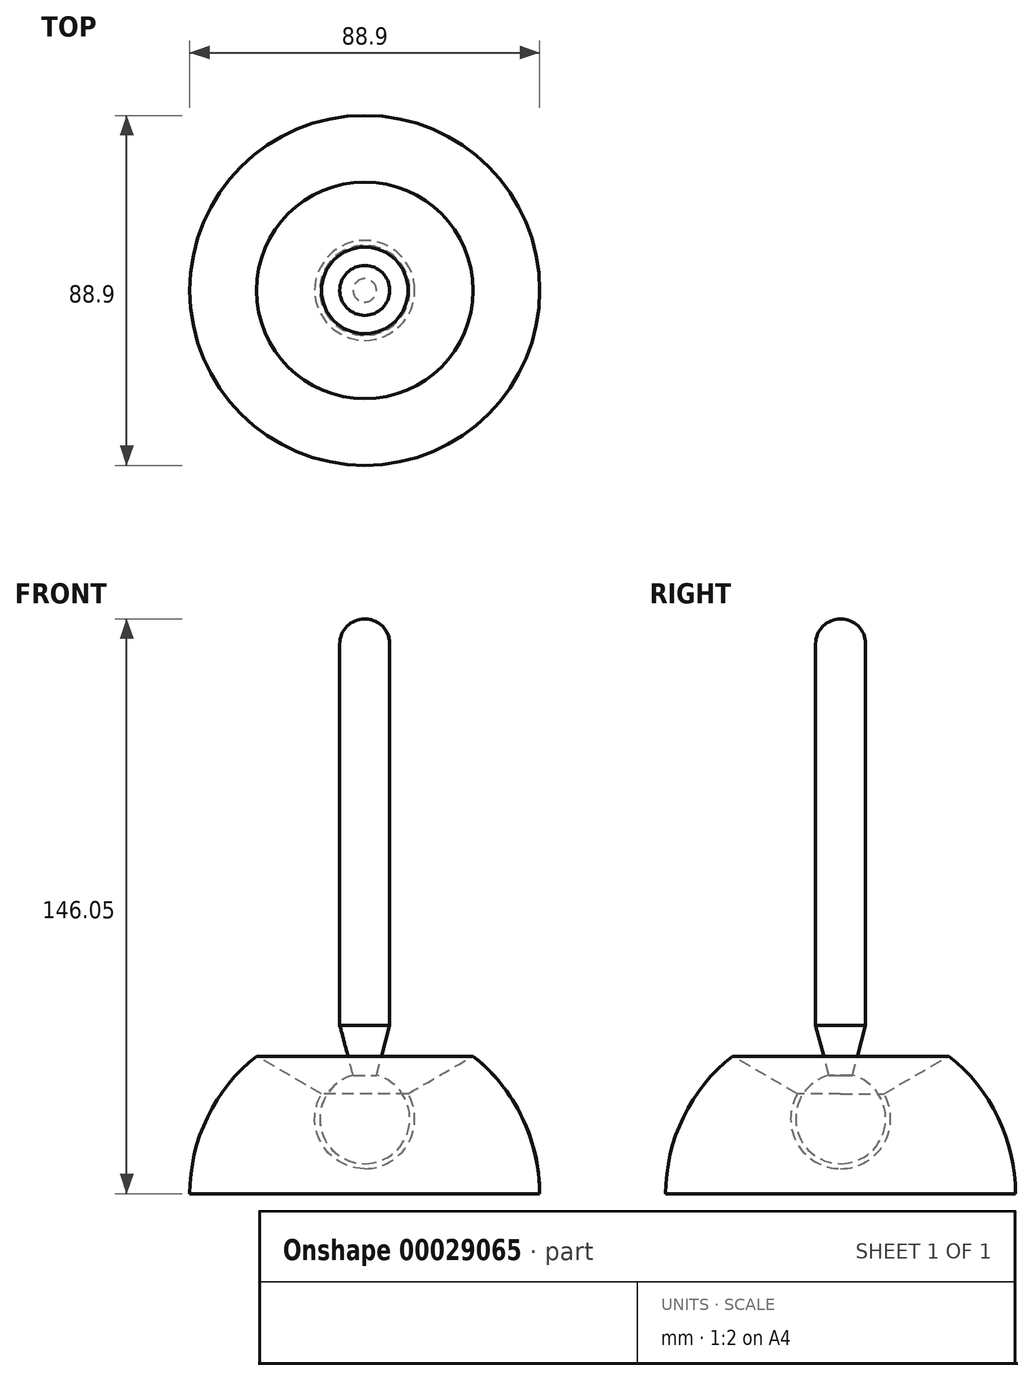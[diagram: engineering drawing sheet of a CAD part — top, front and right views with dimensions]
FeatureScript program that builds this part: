
annotation { "Feature Type Name" : "Feature", "Feature Type Description" : "" }
export const myFeature = defineFeature(function(context is Context, id is Id, definition is map)
    precondition{}
    {
        {
            var Q0;
            Q0=qCreatedBy(makeId("Front.planeOp"),FACE);
            var sketch = newSketch(context, id + "F0", { "sketchPlane" : qUnion([Q0])});
            skArc(sketch, "E0", {"start": v(0, -12.7) * mm, "mid": v(11, -6.35) * mm, "end": v(11, 6.35) * mm});
            skLineSegment(sketch, "E1", {"start": v(11, 6.35) * mm, "end": v(27.5, 15.88) * mm});
            skLineSegment(sketch, "E2", {"start": v(0, -19.05) * mm, "end": v(44.45, -19.05) * mm});
            skArc(sketch, "E3.trimOffspring", {"start": v(44.45, -19.05) * mm, "mid": v(39.99, 0.36) * mm, "end": v(27.5, 15.88) * mm});
            skLineSegment(sketch, "E4", {"start": v(0, -12.7) * mm, "end": v(0, -19.05) * mm});
            skSolve(sketch);
        }
        {
            var Q0;
            Q0=makeQuery(id+"F0.imprint","IMPRINT",FACE,{"disambiguationData":[TD([[makeQuery(id+"F0.imprint","IMPRINT",EDGE,{"derivedFrom":sQuery(id+"F0.wireOp",EDGE,"E0")}),-1.0]])]});
            var Q1;
            Q1=sQuery(id+"F0.wireOp",EDGE,"E4");
            revolve(context, id + "F1", {"entities" : qUnion([Q0]), "axis" : qUnion([Q1]), "revolveType" : RevolveType.FULL});
        }
        {
            var Q0;
            Q0=qCreatedBy(makeId("Front.planeOp"),FACE);
            var sketch = newSketch(context, id + "F2", { "sketchPlane" : qUnion([Q0])});
            skArc(sketch, "E5", {"start": v(0, -11.43) * mm, "mid": v(11.33, -1.5) * mm, "end": v(2.96, 11.04) * mm});
            skLineSegment(sketch, "E6", {"start": v(0, -11.43) * mm, "end": v(0, 127) * mm});
            skLineSegment(sketch, "E7", {"start": v(6.35, 120.65) * mm, "end": v(6.35, 23.7) * mm});
            skLineSegment(sketch, "E8", {"start": v(6.35, 23.7) * mm, "end": v(2.96, 11.04) * mm});
            skArc(sketch, "E9", {"start": v(6.35, 120.65) * mm, "mid": v(4.5, 125.14) * mm, "end": v(0, 127) * mm});
            skSolve(sketch);
        }
        {
            var Q0;
            Q0=makeQuery(id+"F2.imprint","IMPRINT",FACE,{"disambiguationData":[TD([[makeQuery(id+"F2.imprint","IMPRINT",EDGE,{"derivedFrom":sQuery(id+"F2.wireOp",EDGE,"E5")}),1.0]])]});
            var Q1;
            Q1=sQuery(id+"F2.wireOp",EDGE,"E6");
            revolve(context, id + "F3", {"entities" : qUnion([Q0]), "axis" : qUnion([Q1]), "revolveType" : RevolveType.FULL});
        }
    });
